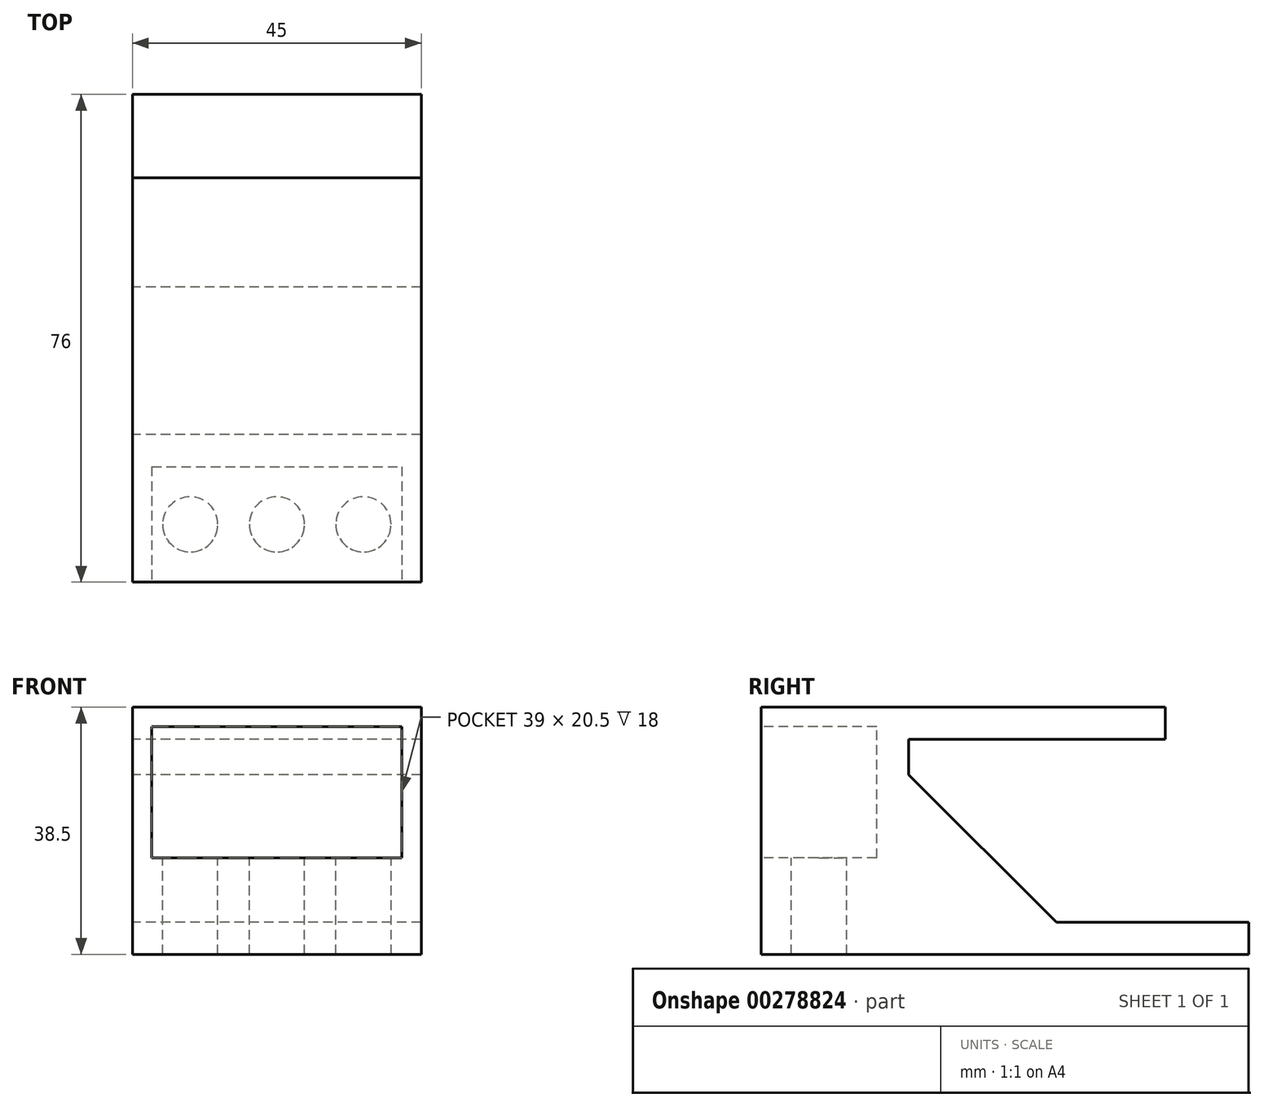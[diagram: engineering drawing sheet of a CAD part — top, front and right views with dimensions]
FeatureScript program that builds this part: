
annotation { "Feature Type Name" : "Feature", "Feature Type Description" : "" }
export const myFeature = defineFeature(function(context is Context, id is Id, definition is map)
    precondition{}
    {
        {
            var Q0;
            Q0=qCreatedBy(makeId("Right.planeOp"),FACE);
            var sketch = newSketch(context, id + "F0", { "sketchPlane" : qUnion([Q0])});
            skLineSegment(sketch, "E0", {"start": v(40, 0) * mm, "end": v(0, 0) * mm});
            skLineSegment(sketch, "E1", {"start": v(0, 0) * mm, "end": v(0, -5.5) * mm});
            skLineSegment(sketch, "E2", {"start": v(0, -5.5) * mm, "end": v(23, -28.5) * mm});
            skLineSegment(sketch, "E3", {"start": v(23, -28.5) * mm, "end": v(53, -28.5) * mm});
            skLineSegment(sketch, "E4", {"start": v(40, 0) * mm, "end": v(40, 5) * mm});
            skLineSegment(sketch, "E5", {"start": v(40, 5) * mm, "end": v(-5, 5) * mm});
            skLineSegment(sketch, "E6", {"start": v(-5, 5) * mm, "end": v(-5, -7.57) * mm});
            skLineSegment(sketch, "E7", {"start": v(-5, -7.57) * mm, "end": v(20.93, -33.5) * mm});
            skLineSegment(sketch, "E8", {"start": v(20.93, -33.5) * mm, "end": v(53, -33.5) * mm});
            skLineSegment(sketch, "E9", {"start": v(53, -33.5) * mm, "end": v(53, -28.5) * mm});
            skLineSegment(sketch, "E10", {"start": v(0, 0) * mm, "end": v(-5, 0) * mm, "construction": true});
            skLineSegment(sketch, "E11", {"start": v(11.5, -17) * mm, "end": v(7.96, -20.54) * mm, "construction": true});
            skSolve(sketch);
        }
        {
            var Q0;
            Q0 = qSketchRegion(id + "F0", true);
            extrude(context, id + "F1", {"entities" : qUnion([Q0]), "endBound" : BoundingType.SYMMETRIC, "depth" : 45 * mm, "offsetDistance" : 25 * mm});
        }
        {
            var Q0;
            Q0=makeQuery(id+"F1.opExtrude","CAP_FACE",FACE,{"disambiguationData":[OSD([sQuery(id+"F0.wireOp",EDGE,"E0"),sQuery(id+"F0.wireOp",EDGE,"E1"),sQuery(id+"F0.wireOp",EDGE,"E2"),sQuery(id+"F0.wireOp",EDGE,"E3"),sQuery(id+"F0.wireOp",EDGE,"E4"),sQuery(id+"F0.wireOp",EDGE,"E5"),sQuery(id+"F0.wireOp",EDGE,"E6"),sQuery(id+"F0.wireOp",EDGE,"E7"),sQuery(id+"F0.wireOp",EDGE,"E8"),sQuery(id+"F0.wireOp",EDGE,"E9")])],"isStart":false});
            var sketch = newSketch(context, id + "F2", { "sketchPlane" : qUnion([Q0])});
            skLineSegment(sketch, "E12.0", {"start": v(-5, 5) * mm, "end": v(-5, -7.57) * mm});
            skLineSegment(sketch, "E12.1", {"start": v(-5, -7.57) * mm, "end": v(20.93, -33.5) * mm});
            skLineSegment(sketch, "E13", {"start": v(-5, 5) * mm, "end": v(-23, 5) * mm});
            skLineSegment(sketch, "E14", {"start": v(-23, 5) * mm, "end": v(-23, -33.5) * mm});
            skLineSegment(sketch, "E15", {"start": v(-23, -33.5) * mm, "end": v(20.93, -33.5) * mm});
            skSolve(sketch);
        }
        {
            var Q0;
            Q0 = qSketchRegion(id + "F2", true);
            var Q1;
            Q1=makeQuery(id+"F1.opExtrude","CAP_FACE",FACE,{"disambiguationData":[OSD([sQuery(id+"F0.wireOp",EDGE,"E0"),sQuery(id+"F0.wireOp",EDGE,"E1"),sQuery(id+"F0.wireOp",EDGE,"E2"),sQuery(id+"F0.wireOp",EDGE,"E3"),sQuery(id+"F0.wireOp",EDGE,"E4"),sQuery(id+"F0.wireOp",EDGE,"E5"),sQuery(id+"F0.wireOp",EDGE,"E6"),sQuery(id+"F0.wireOp",EDGE,"E7"),sQuery(id+"F0.wireOp",EDGE,"E8"),sQuery(id+"F0.wireOp",EDGE,"E9")])],"isStart":true});
            extrude(context, id + "F3", {"entities" : qUnion([Q0]), "operationType" : NewBodyOperationType.ADD, "endBound" : BoundingType.UP_TO_SURFACE, "oppositeDirection" : true, "depth" : 25 * mm, "endBoundEntityFace" : qUnion([Q1]), "offsetDistance" : 25 * mm});
        }
        {
            var Q0;
            Q0=makeQuery(id+"F3.boolean.opBoolean","MERGE",FACE,{"derivedFrom":[makeQuery(id+"F1.opExtrude","SWEPT_FACE",FACE,{"disambiguationData":[OSD([sQuery(id+"F0.wireOp",EDGE,"E5")])]}),makeQuery(id+"F3.opExtrude","SWEPT_FACE",FACE,{"disambiguationData":[OSD([sQuery(id+"F2.wireOp",EDGE,"E13")])]})]});
            var sketch = newSketch(context, id + "F4", { "sketchPlane" : qUnion([Q0])});
            skLineSegment(sketch, "E16", {"start": v(-22.5, -14) * mm, "end": v(22.5, -14) * mm, "construction": true});
            skLineSegment(sketch, "E17", {"start": v(0, 0) * mm, "end": v(0, -23) * mm, "construction": true});
            skCircle(sketch, "E18", {"center": v(0, -14) * mm, "radius": 4.3 * mm});
            skCircle(sketch, "E19", {"center": v(13.5, -14) * mm, "radius": 4.3 * mm});
            skCircle(sketch, "E20.MirrorC", {"center": v(-13.5, -14) * mm, "radius": 4.3 * mm});
            skSolve(sketch);
        }
        {
            var Q0;
            Q0 = qSketchRegion(id + "F4", true);
            extrude(context, id + "F5", {"entities" : qUnion([Q0]), "operationType" : NewBodyOperationType.REMOVE, "endBound" : BoundingType.THROUGH_ALL, "oppositeDirection" : true, "depth" : 25 * mm, "offsetDistance" : 25 * mm});
        }
        {
            var Q0;
            Q0=makeQuery(id+"F3.opExtrude","SWEPT_FACE",FACE,{"disambiguationData":[OSD([sQuery(id+"F2.wireOp",EDGE,"E14")])]});
            var sketch = newSketch(context, id + "F6", { "sketchPlane" : qUnion([Q0])});
            skLineSegment(sketch, "E21", {"start": v(-22.5, -18.5) * mm, "end": v(22.5, -18.5) * mm, "construction": true});
            skLineSegment(sketch, "E22.bottom", {"start": v(-19.5, -18.5) * mm, "end": v(19.5, -18.5) * mm});
            skLineSegment(sketch, "E22.top", {"start": v(-19.5, 2) * mm, "end": v(19.5, 2) * mm});
            skLineSegment(sketch, "E22.left", {"start": v(-19.5, -18.5) * mm, "end": v(-19.5, 2) * mm});
            skLineSegment(sketch, "E22.right", {"start": v(19.5, -18.5) * mm, "end": v(19.5, 2) * mm});
            skLineSegment(sketch, "E23", {"start": v(0, -33.5) * mm, "end": v(0, -19.48) * mm, "construction": true});
            skSolve(sketch);
        }
        {
            var Q0;
            Q0 = qSketchRegion(id + "F6", true);
            extrude(context, id + "F7", {"entities" : qUnion([Q0]), "operationType" : NewBodyOperationType.REMOVE, "oppositeDirection" : true, "depth" : 18 * mm, "offsetDistance" : 25 * mm});
        }
        {
            var Q0;
            Q0 = qSketchRegion(id + "F6", true);
            extrude(context, id + "F8", {"entities" : qUnion([Q0]), "operationType" : NewBodyOperationType.REMOVE, "oppositeDirection" : true, "depth" : 18 * mm, "offsetDistance" : 25 * mm});
        }
        {
            var Q0;
            Q0=makeQuery(id+"F3.boolean.opBoolean","MERGE",FACE,{"derivedFrom":[makeQuery(id+"F1.opExtrude","SWEPT_FACE",FACE,{"disambiguationData":[OSD([sQuery(id+"F0.wireOp",EDGE,"E5")])]}),makeQuery(id+"F3.opExtrude","SWEPT_FACE",FACE,{"disambiguationData":[OSD([sQuery(id+"F2.wireOp",EDGE,"E13")])]})]});
            var sketch = newSketch(context, id + "F9", { "sketchPlane" : qUnion([Q0])});
            skCircle(sketch, "E24.0", {"center": v(-13.5, -14) * mm, "radius": 4.3 * mm});
            skCircle(sketch, "E24.1", {"center": v(0, -14) * mm, "radius": 4.3 * mm});
            skCircle(sketch, "E24.2", {"center": v(13.5, -14) * mm, "radius": 4.3 * mm});
            skSolve(sketch);
        }
        {
            var Q0;
            Q0 = qSketchRegion(id + "F9", true);
            var Q1;
            Q1=makeQuery(id+"F7.boolean.opBoolean","COPY",FACE,{"derivedFrom":makeQuery(id+"F7.opExtrude","SWEPT_FACE",FACE,{"disambiguationData":[OSD([sQuery(id+"F6.wireOp",EDGE,"E22.top")])]})});
            extrude(context, id + "F10", {"entities" : qUnion([Q0]), "operationType" : NewBodyOperationType.ADD, "endBound" : BoundingType.UP_TO_SURFACE, "oppositeDirection" : true, "depth" : 25 * mm, "endBoundEntityFace" : qUnion([Q1]), "offsetDistance" : 25 * mm});
        }
    });
